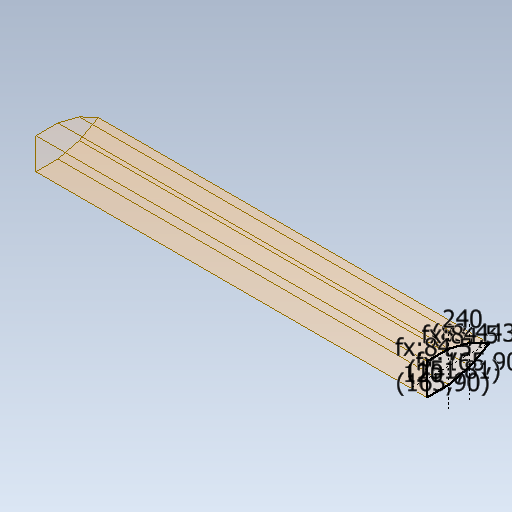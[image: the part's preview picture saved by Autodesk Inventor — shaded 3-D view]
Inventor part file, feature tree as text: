
AUTODESK INVENTOR PART (.ipt)
format: ipt  version: 2020.1 (Build 241239000, 239)  size: 114,688 bytes
history: native  units: mm
features: sketch x2, other x1, sweep x1
ambient origin geometry x8: Origin, YZ Plane, XZ Plane, XY Plane, X Axis, Y Axis, Z Axis, Center Point
bodies: Body1 (feature_tree)
feature tree (4):
  sketch  "Sketch2"  dims[d1=240.0mm d4=0.0mm d5=0.0mm]
  sketch  "Sketch3"  dims[d10=26.495542mm d11=28.955734mm d12=28.955734mm d15=120.0mm d16=84.5mm d18=84.5mm d19=83.443035mm d20=1500.0mm]
  other  "Srf1"
  sweep  "SweepSrf1"
